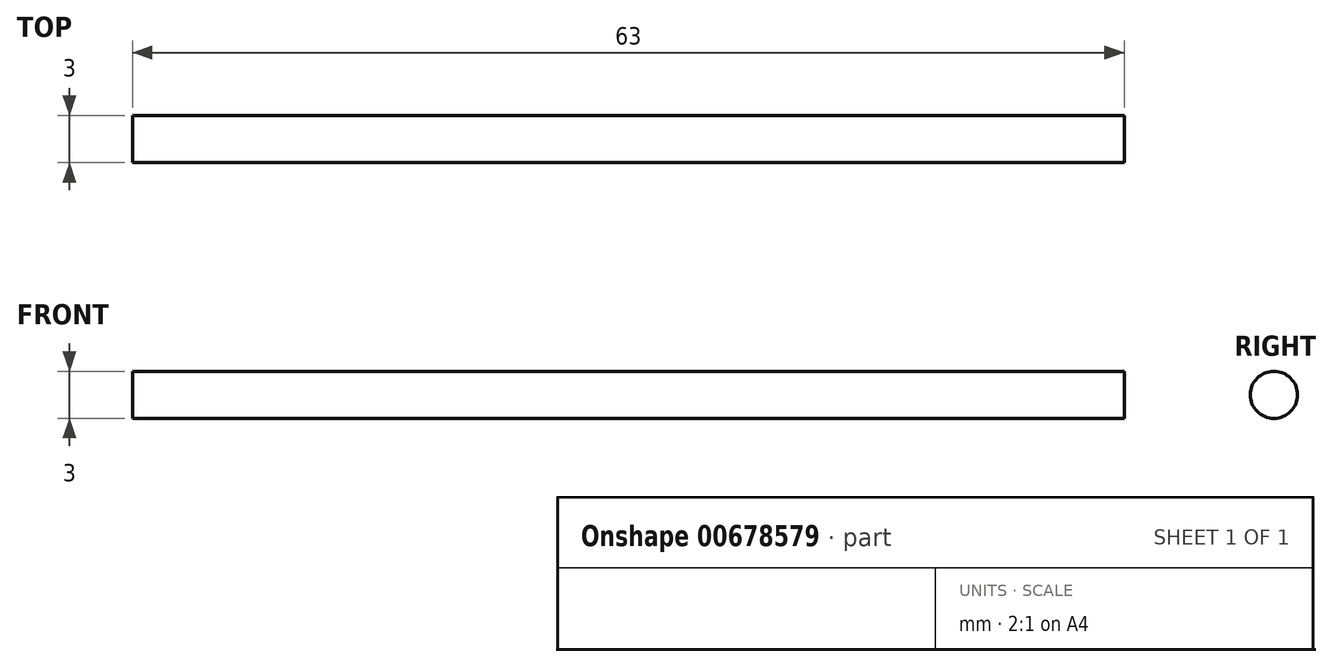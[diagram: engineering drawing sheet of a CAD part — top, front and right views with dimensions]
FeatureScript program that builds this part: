
annotation { "Feature Type Name" : "Feature", "Feature Type Description" : "" }
export const myFeature = defineFeature(function(context is Context, id is Id, definition is map)
    precondition{}
    {
        {
            var Q0;
            Q0=qCreatedBy(makeId("Front.planeOp"),FACE);
            var sketch = newSketch(context, id + "F0", { "sketchPlane" : qUnion([Q0])});
            skLineSegment(sketch, "E0", {"start": v(0, 0) * mm, "end": v(63, 0) * mm});
            skLineSegment(sketch, "E1", {"start": v(0, 0) * mm, "end": v(0, 1.5) * mm});
            skLineSegment(sketch, "E2", {"start": v(0, 1.5) * mm, "end": v(63, 1.5) * mm});
            skLineSegment(sketch, "E3", {"start": v(63, 1.5) * mm, "end": v(63, 0) * mm});
            skSolve(sketch);
        }
        {
            var Q0;
            Q0 = qSketchRegion(id + "F0", true);
            var Q1;
            Q1=sQuery(id+"F0.wireOp",EDGE,"E0");
            revolve(context, id + "F1", {"entities" : qUnion([Q0]), "axis" : qUnion([Q1]), "revolveType" : RevolveType.FULL});
        }
    });
